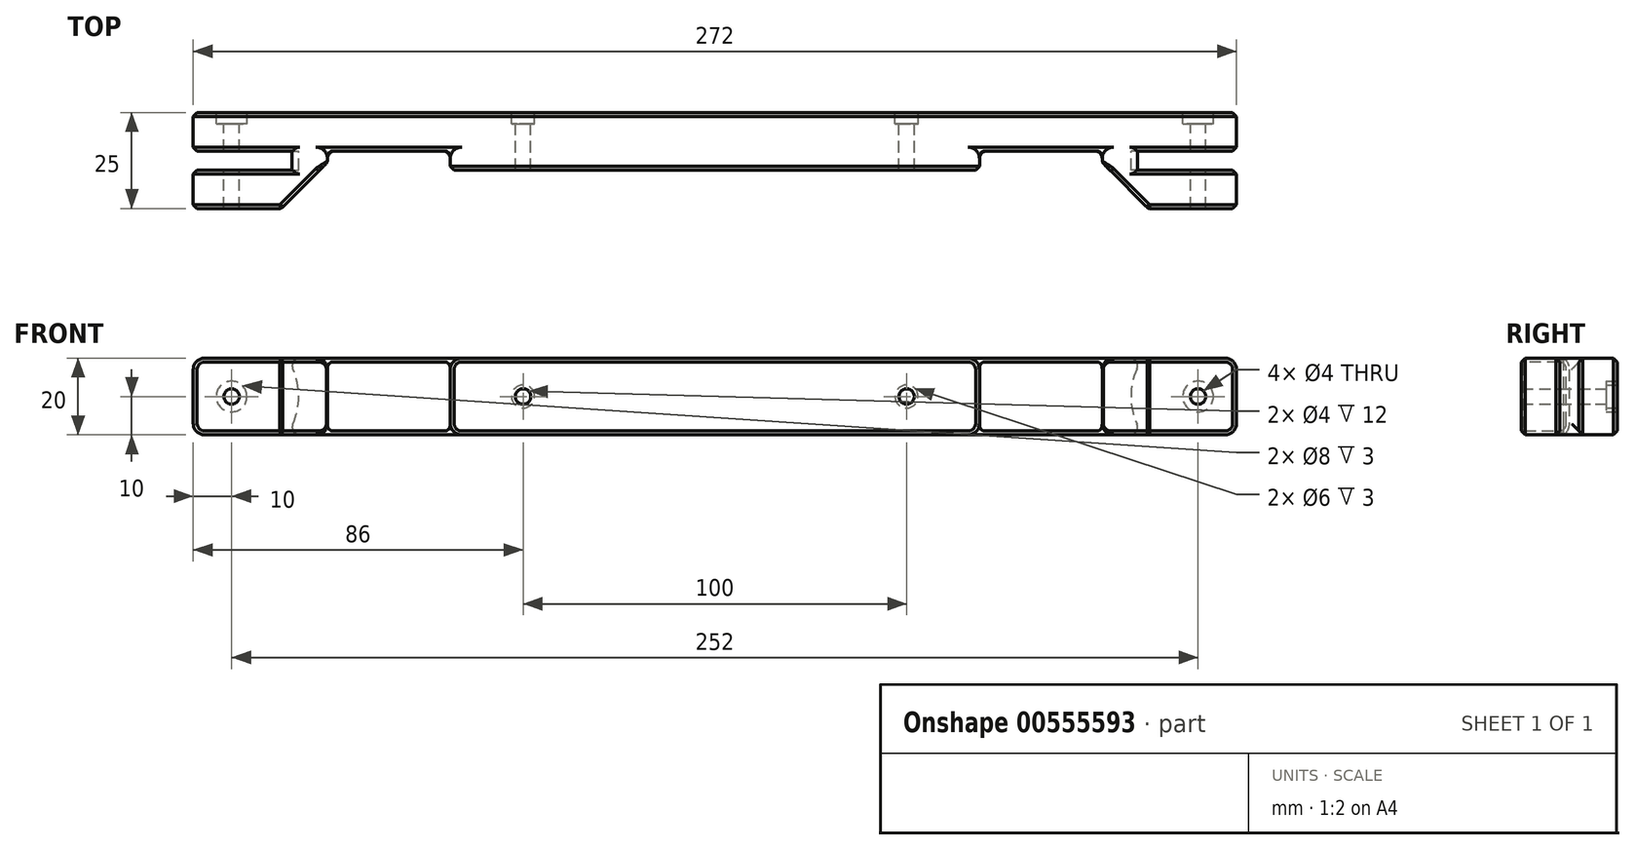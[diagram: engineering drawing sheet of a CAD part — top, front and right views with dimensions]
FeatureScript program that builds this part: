
annotation { "Feature Type Name" : "Feature", "Feature Type Description" : "" }
export const myFeature = defineFeature(function(context is Context, id is Id, definition is map)
    precondition{}
    {
        {
            var Q0;
            Q0=qCreatedBy(makeId("Top.planeOp"),FACE);
            var sketch = newSketch(context, id + "F0", { "sketchPlane" : qUnion([Q0])});
            skLineSegment(sketch, "E0.bottom", {"start": v(-136, 10) * mm, "end": v(0, 10) * mm});
            skLineSegment(sketch, "E0.top", {"start": v(-136, -15) * mm, "end": v(-113, -15) * mm});
            skLineSegment(sketch, "E0.left", {"start": v(-136, 10) * mm, "end": v(-136, 0) * mm});
            skLineSegment(sketch, "E1.top", {"start": v(-69, -5) * mm, "end": v(0, -5) * mm});
            skLineSegment(sketch, "E2.top", {"start": v(-101, 0) * mm, "end": v(-69, 0) * mm});
            skLineSegment(sketch, "E2.right", {"start": v(-69, -5) * mm, "end": v(-69, 0) * mm});
            skLineSegment(sketch, "E3.MirrorCS", {"start": v(-116, 0) * mm, "end": v(-116, -5) * mm});
            skLineSegment(sketch, "E4.MirrorCS", {"start": v(-136, 0) * mm, "end": v(-116, 0) * mm});
            skLineSegment(sketch, "E5.MirrorCS", {"start": v(-136, -5) * mm, "end": v(-116, -5) * mm});
            skLineSegment(sketch, "E6", {"start": v(-101, 0) * mm, "end": v(-101, -3) * mm});
            skLineSegment(sketch, "E7", {"start": v(0, 10) * mm, "end": v(0, -5) * mm});
            skLineSegment(sketch, "E8.trimOffspring", {"start": v(-136, -5) * mm, "end": v(-136, -15) * mm});
            skLineSegment(sketch, "E9", {"start": v(-101, -3) * mm, "end": v(-113, -15) * mm});
            skSolve(sketch);
        }
        {
            var Q0;
            Q0=makeQuery(id+"F0.imprint","IMPRINT",FACE,{"disambiguationData":[TD([[makeQuery(id+"F0.imprint","IMPRINT",EDGE,{"derivedFrom":sQuery(id+"F0.wireOp",EDGE,"E0.bottom")}),-1.0]])]});
            extrude(context, id + "F1", {"entities" : qUnion([Q0]), "depth" : 20 * mm, "offsetDistance" : 25 * mm});
        }
        {
            var Q0;
            Q0=makeQuery(id+"F1.opExtrude","SWEPT_FACE",FACE,{"disambiguationData":[OSD([sQuery(id+"F0.wireOp",EDGE,"E0.bottom")])]});
            var sketch = newSketch(context, id + "F2", { "sketchPlane" : qUnion([Q0])});
            skCircle(sketch, "E10", {"center": v(50, 10) * mm, "radius": 2 * mm});
            skCircle(sketch, "E11.MirrorC", {"center": v(-50, 10) * mm, "radius": 2 * mm});
            skCircle(sketch, "E12", {"center": v(126, 10) * mm, "radius": 2 * mm});
            skCircle(sketch, "E13.MirrorC", {"center": v(-126, 10) * mm, "radius": 2 * mm});
            skLineSegment(sketch, "E14", {"start": v(100, 0) * mm, "end": v(100, 20) * mm, "construction": true});
            skCircle(sketch, "E15", {"center": v(50, 10) * mm, "radius": 3 * mm});
            skCircle(sketch, "E16", {"center": v(126, 10) * mm, "radius": 4 * mm});
            skSolve(sketch);
        }
        {
            var Q0;
            Q0=makeQuery(id+"F2.imprint","IMPRINT",FACE,{"disambiguationData":[TD([[makeQuery(id+"F2.imprint","IMPRINT",EDGE,{"derivedFrom":sQuery(id+"F2.wireOp",EDGE,"E10")}),1.0]])]});
            var Q1;
            Q1=makeQuery(id+"F2.imprint","IMPRINT",FACE,{"disambiguationData":[TD([[makeQuery(id+"F2.imprint","IMPRINT",EDGE,{"derivedFrom":sQuery(id+"F2.wireOp",EDGE,"E11.MirrorC")}),-1.0]])]});
            var Q2;
            Q2=makeQuery(id+"F2.imprint","IMPRINT",FACE,{"disambiguationData":[TD([[makeQuery(id+"F2.imprint","IMPRINT",EDGE,{"derivedFrom":sQuery(id+"F2.wireOp",EDGE,"E13.MirrorC")}),-1.0]])]});
            var Q3;
            Q3=makeQuery(id+"F2.imprint","IMPRINT",FACE,{"disambiguationData":[TD([[makeQuery(id+"F2.imprint","IMPRINT",EDGE,{"derivedFrom":sQuery(id+"F2.wireOp",EDGE,"E12")}),1.0]])]});
            extrude(context, id + "F3", {"entities" : qUnion([Q0, Q1, Q2, Q3]), "operationType" : NewBodyOperationType.REMOVE, "oppositeDirection" : true, "depth" : 25 * mm, "offsetDistance" : 25 * mm});
        }
        {
            var Q0;
            Q0=makeQuery(id+"F2.imprint","IMPRINT",FACE,{"disambiguationData":[TD([[makeQuery(id+"F2.imprint","IMPRINT",EDGE,{"derivedFrom":sQuery(id+"F2.wireOp",EDGE,"E10")}),-1.0]])]});
            var Q1;
            Q1=makeQuery(id+"F2.imprint","IMPRINT",FACE,{"disambiguationData":[TD([[makeQuery(id+"F2.imprint","IMPRINT",EDGE,{"derivedFrom":sQuery(id+"F2.wireOp",EDGE,"E12")}),-1.0]])]});
            extrude(context, id + "F4", {"entities" : qUnion([Q0, Q1]), "operationType" : NewBodyOperationType.REMOVE, "oppositeDirection" : true, "depth" : 3 * mm, "offsetDistance" : 25 * mm});
        }
        {
            var Q0;
            Q0=makeQuery(id+"F1.opExtrude","SWEPT_FACE",FACE,{"disambiguationData":[OSD([sQuery(id+"F0.wireOp",EDGE,"E4.MirrorCS")])]});
            var sketch = newSketch(context, id + "F5", { "sketchPlane" : qUnion([Q0])});
            skCircle(sketch, "E17", {"center": v(-126, 10) * mm, "radius": 17.5 * mm});
            skSolve(sketch);
        }
        {
            var Q0;
            {var subQ0=sQuery(id+"F0.wireOp",EDGE,"E0.right");Q0=makeQuery(id+"F1.opExtrude","CAP_EDGE",EDGE,{"disambiguationData":[OSD([subQ0]),TDD([makeQuery(id+"F0.imprint","IMPRINT",EDGE,{"disambiguationData":[TD([[makeQuery(id+"F0.imprint","INTERSECT",VERTEX,{"derivedFrom":[sQuery(id+"F0.wireOp",EDGE,"E0.bottom"),subQ0]}),-1.0]])],"derivedFrom":subQ0})])],"isStart":true});}
            var Q1;
            {var subQ0=sQuery(id+"F0.wireOp",EDGE,"E0.right");Q1=makeQuery(id+"F1.opExtrude","CAP_EDGE",EDGE,{"disambiguationData":[OSD([subQ0]),TDD([makeQuery(id+"F0.imprint","IMPRINT",EDGE,{"disambiguationData":[TD([[makeQuery(id+"F0.imprint","INTERSECT",VERTEX,{"derivedFrom":[subQ0,sQuery(id+"F0.wireOp",EDGE,"e866c324-1d81-4979-963c-a210c2d08ae6.trimOffspring")]}),1.0]])],"derivedFrom":subQ0})])],"isStart":true});}
            var Q2;
            Q2=makeQuery(id+"F1.opExtrude","CAP_EDGE",EDGE,{"disambiguationData":[OSD([sQuery(id+"F0.wireOp",EDGE,"yvUwwp47-yIZl-wQDH-byZU-GnDJ9XuptdRq.left")])],"isStart":true});
            var Q3;
            {var subQ0=sQuery(id+"F0.wireOp",EDGE,"E0.right");Q3=makeQuery(id+"F1.opExtrude","CAP_EDGE",EDGE,{"disambiguationData":[OSD([subQ0]),TDD([makeQuery(id+"F0.imprint","IMPRINT",EDGE,{"disambiguationData":[TD([[makeQuery(id+"F0.imprint","INTERSECT",VERTEX,{"derivedFrom":[subQ0,sQuery(id+"F0.wireOp",EDGE,"e866c324-1d81-4979-963c-a210c2d08ae6.trimOffspring")]}),1.0]])],"derivedFrom":subQ0})])],"isStart":false});}
            var Q4;
            {var subQ0=sQuery(id+"F0.wireOp",EDGE,"E0.right");Q4=makeQuery(id+"F1.opExtrude","CAP_EDGE",EDGE,{"disambiguationData":[OSD([subQ0]),TDD([makeQuery(id+"F0.imprint","IMPRINT",EDGE,{"disambiguationData":[TD([[makeQuery(id+"F0.imprint","INTERSECT",VERTEX,{"derivedFrom":[sQuery(id+"F0.wireOp",EDGE,"E0.bottom"),subQ0]}),-1.0]])],"derivedFrom":subQ0})])],"isStart":false});}
            var Q5;
            Q5=makeQuery(id+"F1.opExtrude","CAP_EDGE",EDGE,{"disambiguationData":[OSD([sQuery(id+"F0.wireOp",EDGE,"yvUwwp47-yIZl-wQDH-byZU-GnDJ9XuptdRq.left")])],"isStart":false});
            var Q6;
            Q6=makeQuery(id+"F1.opExtrude","CAP_EDGE",EDGE,{"disambiguationData":[OSD([sQuery(id+"F0.wireOp",EDGE,"yvUwwp47-yIZl-wQDH-byZU-GnDJ9XuptdRq.right")])],"isStart":false});
            var Q7;
            Q7=makeQuery(id+"F1.opExtrude","CAP_EDGE",EDGE,{"disambiguationData":[OSD([sQuery(id+"F0.wireOp",EDGE,"yvUwwp47-yIZl-wQDH-byZU-GnDJ9XuptdRq.right")])],"isStart":true});
            var Q8;
            Q8=makeQuery(id+"F1.opExtrude","CAP_EDGE",EDGE,{"disambiguationData":[OSD([sQuery(id+"F0.wireOp",EDGE,"E2.left")])],"isStart":false});
            var Q9;
            Q9=makeQuery(id+"F1.opExtrude","CAP_EDGE",EDGE,{"disambiguationData":[OSD([sQuery(id+"F0.wireOp",EDGE,"E2.left")])],"isStart":true});
            var Q10;
            Q10=makeQuery(id+"F1.opExtrude","CAP_EDGE",EDGE,{"disambiguationData":[OSD([sQuery(id+"F0.wireOp",EDGE,"E2.right")])],"isStart":false});
            var Q11;
            {var subQ0=sQuery(id+"F0.wireOp",EDGE,"E0.left");Q11=makeQuery(id+"F1.opExtrude","CAP_EDGE",EDGE,{"disambiguationData":[OSD([subQ0]),TDD([makeQuery(id+"F0.imprint","IMPRINT",EDGE,{"disambiguationData":[TD([[makeQuery(id+"F0.imprint","INTERSECT",VERTEX,{"derivedFrom":[sQuery(id+"F0.wireOp",EDGE,"E0.top"),subQ0]}),1.0]])],"derivedFrom":subQ0})])],"isStart":false});}
            var Q12;
            {var subQ0=sQuery(id+"F0.wireOp",EDGE,"E0.left");Q12=makeQuery(id+"F1.opExtrude","CAP_EDGE",EDGE,{"disambiguationData":[OSD([subQ0]),TDD([makeQuery(id+"F0.imprint","IMPRINT",EDGE,{"disambiguationData":[TD([[makeQuery(id+"F0.imprint","INTERSECT",VERTEX,{"derivedFrom":[sQuery(id+"F0.wireOp",EDGE,"E0.bottom"),subQ0]}),-1.0]])],"derivedFrom":subQ0})])],"isStart":false});}
            var Q13;
            Q13=makeQuery(id+"F1.opExtrude","CAP_EDGE",EDGE,{"disambiguationData":[OSD([sQuery(id+"F0.wireOp",EDGE,"E2.right")])],"isStart":true});
            var Q14;
            {var subQ0=sQuery(id+"F0.wireOp",EDGE,"E0.left");Q14=makeQuery(id+"F1.opExtrude","CAP_EDGE",EDGE,{"disambiguationData":[OSD([subQ0]),TDD([makeQuery(id+"F0.imprint","IMPRINT",EDGE,{"disambiguationData":[TD([[makeQuery(id+"F0.imprint","INTERSECT",VERTEX,{"derivedFrom":[sQuery(id+"F0.wireOp",EDGE,"E0.top"),subQ0]}),1.0]])],"derivedFrom":subQ0})])],"isStart":true});}
            var Q15;
            {var subQ0=sQuery(id+"F0.wireOp",EDGE,"E0.left");Q15=makeQuery(id+"F1.opExtrude","CAP_EDGE",EDGE,{"disambiguationData":[OSD([subQ0]),TDD([makeQuery(id+"F0.imprint","IMPRINT",EDGE,{"disambiguationData":[TD([[makeQuery(id+"F0.imprint","INTERSECT",VERTEX,{"derivedFrom":[sQuery(id+"F0.wireOp",EDGE,"E0.bottom"),subQ0]}),-1.0]])],"derivedFrom":subQ0})])],"isStart":true});}
            var Q16;
            Q16=makeQuery(id+"F1.opExtrude","CAP_EDGE",EDGE,{"disambiguationData":[OSD([sQuery(id+"F0.wireOp",EDGE,"E8.trimOffspring")])],"isStart":true});
            var Q17;
            Q17=makeQuery(id+"F1.opExtrude","CAP_EDGE",EDGE,{"disambiguationData":[OSD([sQuery(id+"F0.wireOp",EDGE,"E8.trimOffspring")])],"isStart":false});
            var Q18;
            Q18=makeQuery(id+"F1.opExtrude","CAP_EDGE",EDGE,{"disambiguationData":[OSD([sQuery(id+"F0.wireOp",EDGE,"E6")])],"isStart":false});
            var Q19;
            Q19=makeQuery(id+"F1.opExtrude","CAP_EDGE",EDGE,{"disambiguationData":[OSD([sQuery(id+"F0.wireOp",EDGE,"E6")])],"isStart":true});
            fillet(context, id + "F6", {"entities" : qUnion([Q0, Q1, Q2, Q3, Q4, Q5, Q6, Q7, Q8, Q9, Q10, Q11, Q12, Q13, Q14, Q15, Q16, Q17, Q18, Q19]), "radius" : 3 * mm, "tangentPropagation" : true, "allowEdgeOverflow" : false});
        }
        {
            var Q0;
            Q0=makeQuery(id+"F5.imprint","IMPRINT",FACE,{"disambiguationData":[TD([[makeQuery(id+"F5.imprint","IMPRINT",EDGE,{"derivedFrom":sQuery(id+"F5.wireOp",EDGE,"E17")}),1.0]])]});
            extrude(context, id + "F7", {"entities" : qUnion([Q0]), "operationType" : NewBodyOperationType.REMOVE, "depth" : 5 * mm, "offsetDistance" : 25 * mm});
        }
        {
            var Q0;
            Q0=makeQuery(id+"F1.opExtrude","CAP_EDGE",EDGE,{"disambiguationData":[OSD([sQuery(id+"F0.wireOp",EDGE,"E0.top")])],"isStart":true});
            var Q1;
            Q1=makeQuery(id+"F1.opExtrude","CAP_EDGE",EDGE,{"disambiguationData":[OSD([sQuery(id+"F0.wireOp",EDGE,"e866c324-1d81-4979-963c-a210c2d08ae6.trimOffspring")])],"isStart":true});
            var Q2;
            Q2=makeQuery(id+"F1.opExtrude","CAP_EDGE",EDGE,{"disambiguationData":[OSD([sQuery(id+"F0.wireOp",EDGE,"cfa3b29f-h4Zj-4f0n-OHBq-HIu5c52tocqQ.bottom")])],"isStart":true});
            var Q3;
            Q3=makeQuery(id+"F1.opExtrude","CAP_EDGE",EDGE,{"disambiguationData":[OSD([sQuery(id+"F0.wireOp",EDGE,"E4.MirrorCS")])],"isStart":true});
            var Q4;
            Q4=makeQuery(id+"F1.opExtrude","CAP_EDGE",EDGE,{"disambiguationData":[OSD([sQuery(id+"F0.wireOp",EDGE,"E5.MirrorCS")])],"isStart":true});
            var Q5;
            Q5=makeQuery(id+"F1.opExtrude","CAP_EDGE",EDGE,{"disambiguationData":[OSD([sQuery(id+"F0.wireOp",EDGE,"cfa3b29f-h4Zj-4f0n-OHBq-HIu5c52tocqQ.top")])],"isStart":true});
            var Q6;
            Q6=makeQuery(id+"F1.opExtrude","CAP_EDGE",EDGE,{"disambiguationData":[OSD([sQuery(id+"F0.wireOp",EDGE,"E0.bottom")])],"isStart":true});
            var Q7;
            Q7=makeQuery(id+"F1.opExtrude","CAP_EDGE",EDGE,{"disambiguationData":[OSD([sQuery(id+"F0.wireOp",EDGE,"E1.top")])],"isStart":true});
            var Q8;
            Q8=makeQuery(id+"F1.opExtrude","CAP_EDGE",EDGE,{"disambiguationData":[OSD([sQuery(id+"F0.wireOp",EDGE,"yvUwwp47-yIZl-wQDH-byZU-GnDJ9XuptdRq.top")])],"isStart":true});
            var Q9;
            Q9=makeQuery(id+"F1.opExtrude","CAP_EDGE",EDGE,{"disambiguationData":[OSD([sQuery(id+"F0.wireOp",EDGE,"E2.top")])],"isStart":true});
            var Q10;
            Q10=makeQuery(id+"F1.opExtrude","CAP_EDGE",EDGE,{"disambiguationData":[OSD([sQuery(id+"F0.wireOp",EDGE,"E2.top")])],"isStart":false});
            var Q11;
            Q11=makeQuery(id+"F1.opExtrude","CAP_EDGE",EDGE,{"disambiguationData":[OSD([sQuery(id+"F0.wireOp",EDGE,"yvUwwp47-yIZl-wQDH-byZU-GnDJ9XuptdRq.top")])],"isStart":false});
            chamfer(context, id + "F8", {"entities" : qUnion([Q0, Q1, Q2, Q3, Q4, Q5, Q6, Q7, Q8, Q9, Q10, Q11]), "width" : 1 * mm, "tangentPropagation" : true});
        }
        {
            var Q0;
            Q0=makeQuery(id+"F1.opExtrude","SWEPT_EDGE",EDGE,{"disambiguationData":[OSD([sQuery(id+"F0.wireOp",EDGE,"E2.top"),sQuery(id+"F0.wireOp",EDGE,"E6")])]});
            var Q1;
            Q1=makeQuery(id+"F1.opExtrude","SWEPT_EDGE",EDGE,{"disambiguationData":[OSD([sQuery(id+"F0.wireOp",EDGE,"E2.top"),sQuery(id+"F0.wireOp",EDGE,"E2.right")])]});
            fillet(context, id + "F9", {"entities" : qUnion([Q0, Q1]), "radius" : 2 * mm, "tangentPropagation" : true, "allowEdgeOverflow" : false});
        }
        {
            var Q0;
            Q0=makeQuery(id+"F7.boolean.opBoolean","INTERSECT",EDGE,{"derivedFrom":[makeQuery(id+"F1.opExtrude","CAP_FACE",FACE,{"disambiguationData":[OSD([sQuery(id+"F0.wireOp",EDGE,"E0.bottom"),sQuery(id+"F0.wireOp",EDGE,"E0.top"),sQuery(id+"F0.wireOp",EDGE,"E0.left"),sQuery(id+"F0.wireOp",EDGE,"E1.top"),sQuery(id+"F0.wireOp",EDGE,"E2.top"),sQuery(id+"F0.wireOp",EDGE,"E2.right"),sQuery(id+"F0.wireOp",EDGE,"E3.MirrorCS"),sQuery(id+"F0.wireOp",EDGE,"E4.MirrorCS"),sQuery(id+"F0.wireOp",EDGE,"E5.MirrorCS"),sQuery(id+"F0.wireOp",EDGE,"E6"),sQuery(id+"F0.wireOp",EDGE,"E7"),sQuery(id+"F0.wireOp",EDGE,"E8.trimOffspring")])],"isStart":true}),makeQuery(id+"F7.opExtrude","SWEPT_FACE",FACE,{"disambiguationData":[OSD([sQuery(id+"F5.wireOp",EDGE,"E17")])]})]});
            var Q1;
            Q1=makeQuery(id+"F7.boolean.opBoolean","INTERSECT",EDGE,{"derivedFrom":[makeQuery(id+"F1.opExtrude","CAP_FACE",FACE,{"disambiguationData":[OSD([sQuery(id+"F0.wireOp",EDGE,"E0.bottom"),sQuery(id+"F0.wireOp",EDGE,"E0.top"),sQuery(id+"F0.wireOp",EDGE,"E0.left"),sQuery(id+"F0.wireOp",EDGE,"E1.top"),sQuery(id+"F0.wireOp",EDGE,"E2.top"),sQuery(id+"F0.wireOp",EDGE,"E2.right"),sQuery(id+"F0.wireOp",EDGE,"E3.MirrorCS"),sQuery(id+"F0.wireOp",EDGE,"E4.MirrorCS"),sQuery(id+"F0.wireOp",EDGE,"E5.MirrorCS"),sQuery(id+"F0.wireOp",EDGE,"E6"),sQuery(id+"F0.wireOp",EDGE,"E7"),sQuery(id+"F0.wireOp",EDGE,"E8.trimOffspring")])],"isStart":false}),makeQuery(id+"F7.opExtrude","SWEPT_FACE",FACE,{"disambiguationData":[OSD([sQuery(id+"F5.wireOp",EDGE,"E17")])]})]});
            fillet(context, id + "F10", {"entities" : qUnion([Q0, Q1]), "radius" : 2 * mm, "tangentPropagation" : true, "allowEdgeOverflow" : false});
        }
        {
            var Q0;
            Q0=makeQuery(id+"F1.opExtrude","SWEPT_FACE",FACE,{"disambiguationData":[OSD([sQuery(id+"F0.wireOp",EDGE,"E9")])]});
            chamfer(context, id + "F11", {"entities" : qUnion([Q0]), "width" : 1 * mm, "tangentPropagation" : true});
        }
        {
            var Q0;
            Q0=makeQuery(id+"F1.opExtrude","SWEPT_BODY",BODY,{"disambiguationData":[OSD([sQuery(id+"F0.wireOp",EDGE,"E0.bottom"),sQuery(id+"F0.wireOp",EDGE,"E0.top"),sQuery(id+"F0.wireOp",EDGE,"E0.left"),sQuery(id+"F0.wireOp",EDGE,"E1.top"),sQuery(id+"F0.wireOp",EDGE,"E2.top"),sQuery(id+"F0.wireOp",EDGE,"E2.right"),sQuery(id+"F0.wireOp",EDGE,"E3.MirrorCS"),sQuery(id+"F0.wireOp",EDGE,"E4.MirrorCS"),sQuery(id+"F0.wireOp",EDGE,"E5.MirrorCS"),sQuery(id+"F0.wireOp",EDGE,"E6"),sQuery(id+"F0.wireOp",EDGE,"E7"),sQuery(id+"F0.wireOp",EDGE,"E8.trimOffspring")])]});
            var Q1;
            Q1=qCreatedBy(makeId("Right.planeOp"),FACE);
            mirror(context, id + "F12", {"operationType" : NewBodyOperationType.ADD, "entities" : qUnion([Q0]), "mirrorPlane" : qUnion([Q1])});
        }
    });
